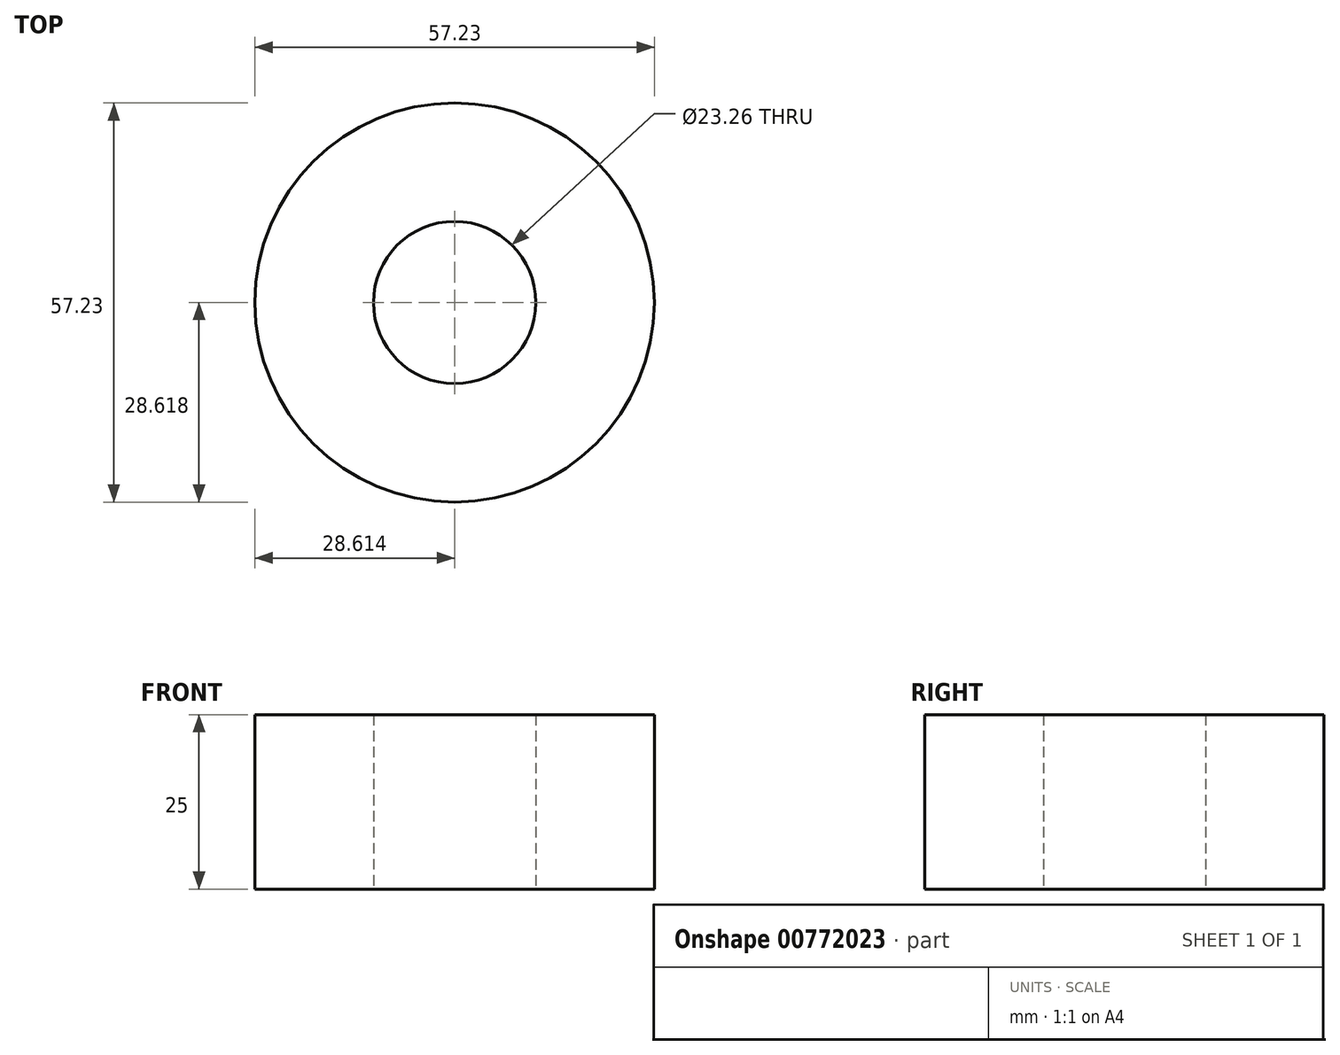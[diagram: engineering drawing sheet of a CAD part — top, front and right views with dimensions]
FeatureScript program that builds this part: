
annotation { "Feature Type Name" : "Feature", "Feature Type Description" : "" }
export const myFeature = defineFeature(function(context is Context, id is Id, definition is map)
    precondition{}
    {
        {
            var Q0;
            Q0=qCreatedBy(makeId("Top.planeOp"),FACE);
            var sketch = newSketch(context, id + "F0", { "sketchPlane" : qUnion([Q0])});
            skCircle(sketch, "E0", {"center": v(-26.92, 35.87) * mm, "radius": 28.62 * mm});
            skCircle(sketch, "E1", {"center": v(-26.92, 35.87) * mm, "radius": 11.63 * mm});
            skSolve(sketch);
        }
        {
            var Q0;
            Q0 = qSketchRegion(id + "F0", true);
            extrude(context, id + "F1", {"entities" : qUnion([Q0]), "depth" : 25 * mm, "offsetDistance" : 25 * mm});
        }
    });
